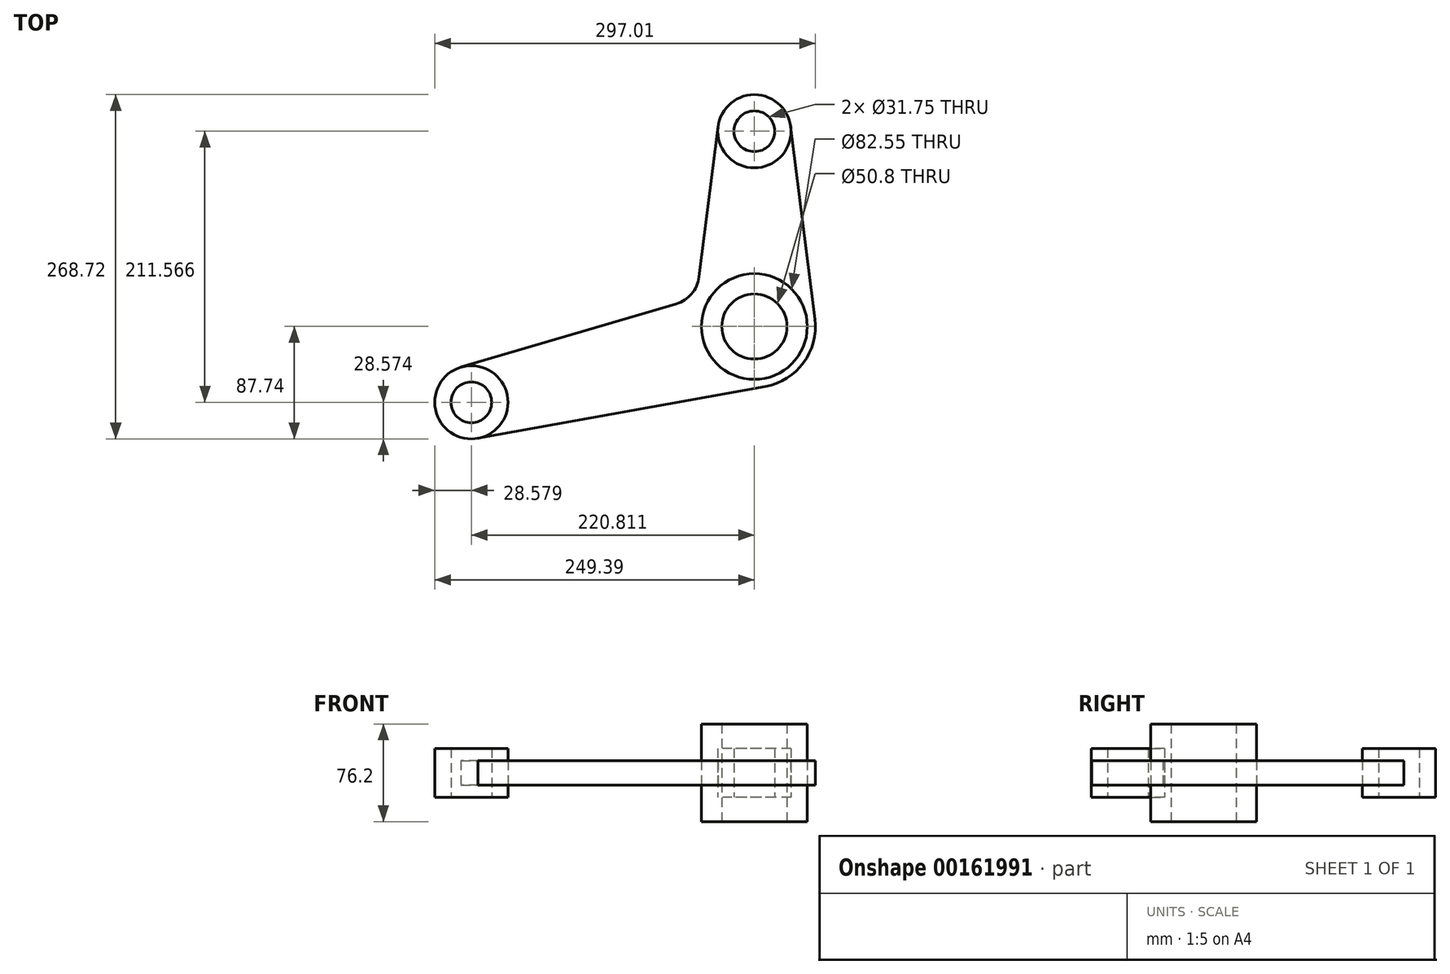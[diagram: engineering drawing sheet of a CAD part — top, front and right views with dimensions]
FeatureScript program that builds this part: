
annotation { "Feature Type Name" : "Feature", "Feature Type Description" : "" }
export const myFeature = defineFeature(function(context is Context, id is Id, definition is map)
    precondition{}
    {
        {
            var Q0;
            Q0=qCreatedBy(makeId("Top.planeOp"),FACE);
            var sketch = newSketch(context, id + "F0", { "sketchPlane" : qUnion([Q0])});
            skCircle(sketch, "E0", {"center": v(0, 0) * mm, "radius": 41.28 * mm});
            skCircle(sketch, "E1", {"center": v(0, 0) * mm, "radius": 25.4 * mm});
            skLineSegment(sketch, "E2", {"start": v(0, 0) * mm, "end": v(0, 152.4) * mm, "construction": true});
            skCircle(sketch, "E3", {"center": v(0, 152.4) * mm, "radius": 28.58 * mm});
            skLineSegment(sketch, "E4", {"start": v(47.25, 5.95) * mm, "end": v(28.35, 155.97) * mm});
            skLineSegment(sketch, "E5", {"start": v(0, 0) * mm, "end": v(-220.81, -59.17) * mm, "construction": true});
            skCircle(sketch, "E6", {"center": v(-220.81, -59.17) * mm, "radius": 28.58 * mm});
            skLineSegment(sketch, "E7", {"start": v(8.45, -46.87) * mm, "end": v(-215.74, -87.29) * mm});
            skArc(sketch, "E8.trimOffspring", {"start": v(8.45, -46.87) * mm, "mid": v(38.38, -28.2) * mm, "end": v(47.25, 5.95) * mm});
            skCircle(sketch, "E9", {"center": v(0, 152.4) * mm, "radius": 15.88 * mm});
            skCircle(sketch, "E10", {"center": v(-220.81, -59.17) * mm, "radius": 15.88 * mm});
            skLineSegment(sketch, "E11", {"start": v(-28.35, 155.97) * mm, "end": v(-43.11, 38.8) * mm});
            skLineSegment(sketch, "E12", {"start": v(-228.88, -31.75) * mm, "end": v(-61.14, 17.6) * mm});
            skPoint(sketch, "E13.visualSharp", {"position": v(-45.2, 22.3) * mm});
            skArc(sketch, "E13.filletArc", {"start": v(-61.14, 17.6) * mm, "mid": v(-48.97, 25.51) * mm, "end": v(-43.11, 38.8) * mm});
            skSolve(sketch);
        }
        {
            var Q0;
            Q0=makeQuery(id+"F0.imprint","IMPRINT",FACE,{"disambiguationData":[TD([[makeQuery(id+"F0.imprint","IMPRINT",EDGE,{"derivedFrom":sQuery(id+"F0.wireOp",EDGE,"E0")}),1.0]])]});
            extrude(context, id + "F1", {"entities" : qUnion([Q0]), "endBound" : BoundingType.SYMMETRIC, "depth" : 76.2 * mm});
        }
        {
            var Q0;
            Q0=makeQuery(id+"F0.imprint","IMPRINT",FACE,{"disambiguationData":[TD([[makeQuery(id+"F0.imprint","IMPRINT",EDGE,{"derivedFrom":sQuery(id+"F0.wireOp",EDGE,"E9")}),-1.0]])]});
            var Q1;
            Q1=makeQuery(id+"F0.imprint","IMPRINT",FACE,{"disambiguationData":[TD([[makeQuery(id+"F0.imprint","IMPRINT",EDGE,{"derivedFrom":sQuery(id+"F0.wireOp",EDGE,"E10")}),-1.0]])]});
            extrude(context, id + "F2", {"entities" : qUnion([Q0, Q1]), "endBound" : BoundingType.SYMMETRIC, "depth" : 38.1 * mm});
        }
        {
            var Q0;
            Q0=makeQuery(id+"F0.imprint","IMPRINT",FACE,{"disambiguationData":[TD([[makeQuery(id+"F0.imprint","IMPRINT",EDGE,{"derivedFrom":sQuery(id+"F0.wireOp",EDGE,"E0")}),-1.0]])]});
            extrude(context, id + "F3", {"entities" : qUnion([Q0]), "endBound" : BoundingType.SYMMETRIC, "depth" : 19.05 * mm});
        }
    });
